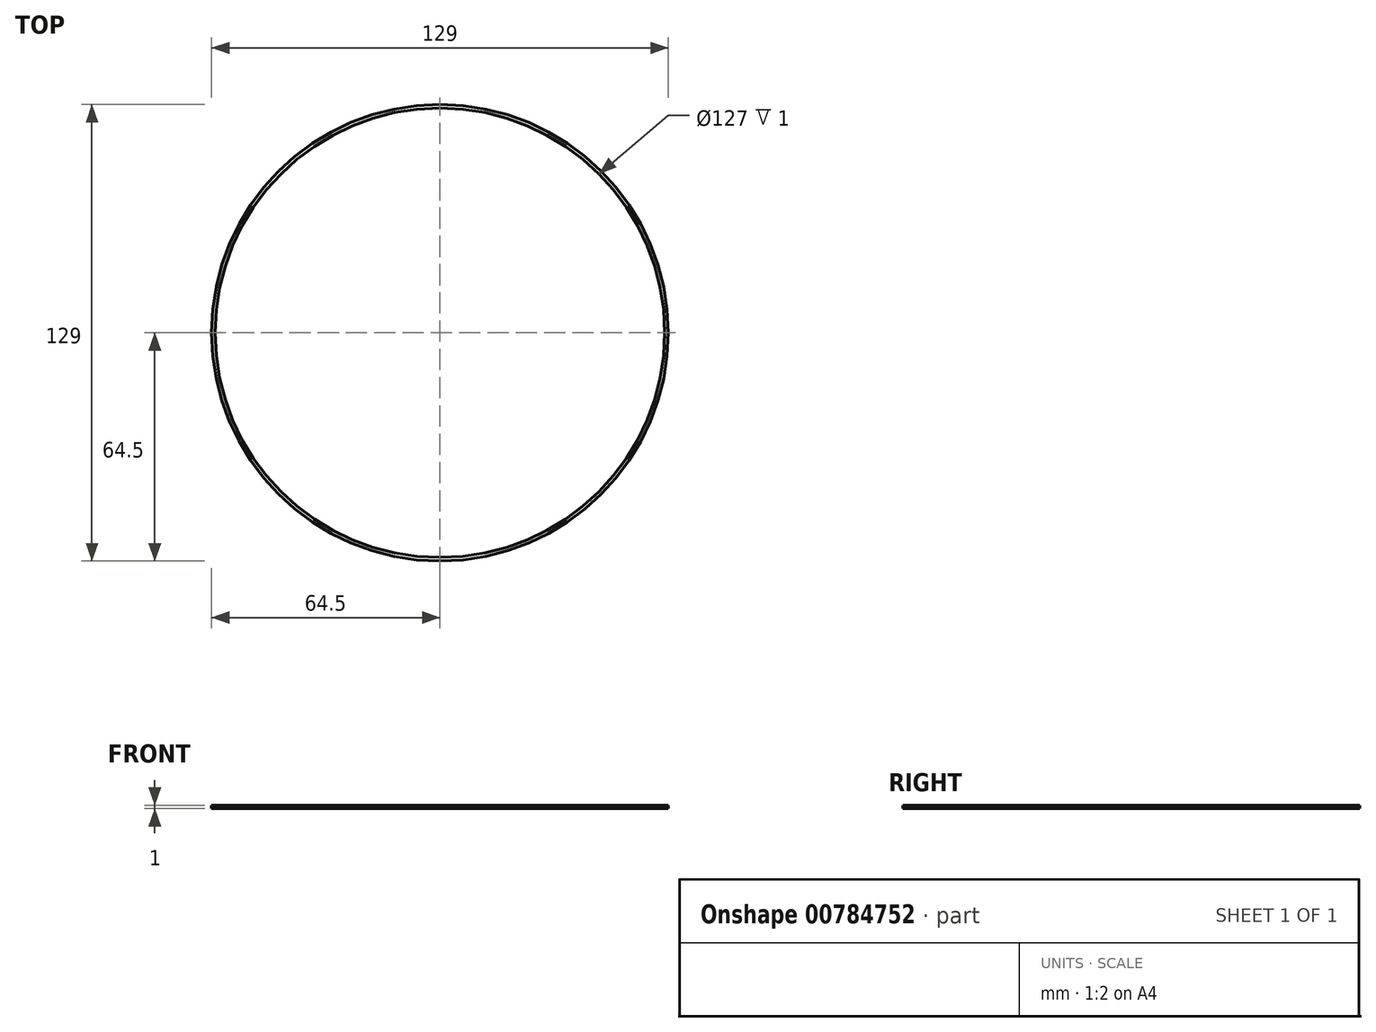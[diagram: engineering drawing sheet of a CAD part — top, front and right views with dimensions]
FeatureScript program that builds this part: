
annotation { "Feature Type Name" : "Feature", "Feature Type Description" : "" }
export const myFeature = defineFeature(function(context is Context, id is Id, definition is map)
    precondition{}
    {
        {
            var Q0;
            Q0=qCreatedBy(makeId("Top.planeOp"),FACE);
            var sketch = newSketch(context, id + "F0", { "sketchPlane" : qUnion([Q0])});
            skCircle(sketch, "E0", {"center": v(0, 0) * mm, "radius": 64.5 * mm});
            skCircle(sketch, "E1", {"center": v(0, 0) * mm, "radius": 63.5 * mm});
            skSolve(sketch);
        }
        {
            var Q0;
            Q0 = qSketchRegion(id + "F0", true);
            extrude(context, id + "F1", {"entities" : qUnion([Q0]), "depth" : 1 * mm, "offsetDistance" : 25 * mm});
        }
    });
